# Revit family: QF_COMENDA_6C201X_6C201XDDPS_CAT
name_source: partatom
category: Attrezzature speciali
units: mm (PartAtom-declared; Revit-internal decimal feet)

## family parameters
Basato su piano di lavoro = No
Condiviso = No
Numero OmniClass = 23.40.40.14
Punto di calcolo locali = No
Quota connettore circolare = Usa diametro
Sempre verticale = Sì
Taglio con vuoti quando caricato = No
Tipo di parte = Normale
Titolo OmniClass = Food Service Equipment

## types (6) — shared parameters
Altezza = 1460 mm  [stored 4.79003 ft]
Altezza allacciamento elettrico da pavimento finito = 160 mm  [stored 0.524934 ft]
Altezza da terra raccordo acqua calda = 210 mm  [stored 0.688976 ft]
Altezza dello scarico diretto acqua da pavimento finito = 160 mm  [stored 0.524934 ft]
Corrente di funzionamento normale = 15 A
Diametro dello scarico diretto di acqua = 1 1/2"
Diametro raccordo acqua calda = 1"
Fase = 3
Frequenza = 50 Hz
Lunghezza = 625 mm  [stored 2.05052 ft]
Numero dei poli = 3
Peso netto = 118.00 kg
Potenza elettrica = 10100 W
Pressione minima acqua calda = 2000.0 Pa
Produttore = COMENDA
Profondità = 740 mm  [stored 2.42782 ft]
Protezione contro le sovracorrenti = 20 A
Temperatura raccomandata per acqua calda = 50 °C
Tensione = 400 V
URL = www.comenda.eu
URL catalogo = https://comenda.eu
zero-valued in all types: Prospetto di default

## per-type parameters (varying)
| type | Descrizione | Modello |
| 6C2010 | MULTIPOWER PASS THROUGH DISHWASHER WITH CRC PRODUCTION BASKETS/HOUR 48 | PC09 |
| 6C2010DDPS | MULTIPOWER PASS THROUGH DISHWASHER WITH CRC, DRAIN PUMP, DETERGENT DOSING PUMP PRODUCTION BASKETS/HOUR 48 | PC09+ |
| 6C2011 | MULTIPOWER PASS THROUGH DISHWASHER WITH RCD PRODUCTION BASKETS/HOUR 48 | PC09 R |
| 6C2011DDPS | MULTIPOWER PASS THROUGH DISHWASHER WITH RCD, DRAIN PUMP, DETERGENT DOSING PUMP PRODUCTION BASKETS/HOUR 48 | PC09 R+ |
| 6C2012 | MULTIPOWER PASS THROUGH DISHWASHER WITH WATER SOFTENER, RCD, PRODUCTION BASKETS/HOUR 48 | PC09 RA |
| 6C2012DDPS | MULTIPOWER PASS THROUGH DISHWASHER WITH WATER SOFTENER, RCD, DRAIN PUMP, DETERGENT DOSING PUMP PRODUCTION BASKETS/HOUR 48 | PC09 RA+ |

note: [stored X ft] marks values corroborated as IEEE doubles in the binary element streams (Revit-internal decimal feet)

## geometry (parser evidence)
native form markers: Sweep x4
no freeform markers — native parametric forms only
